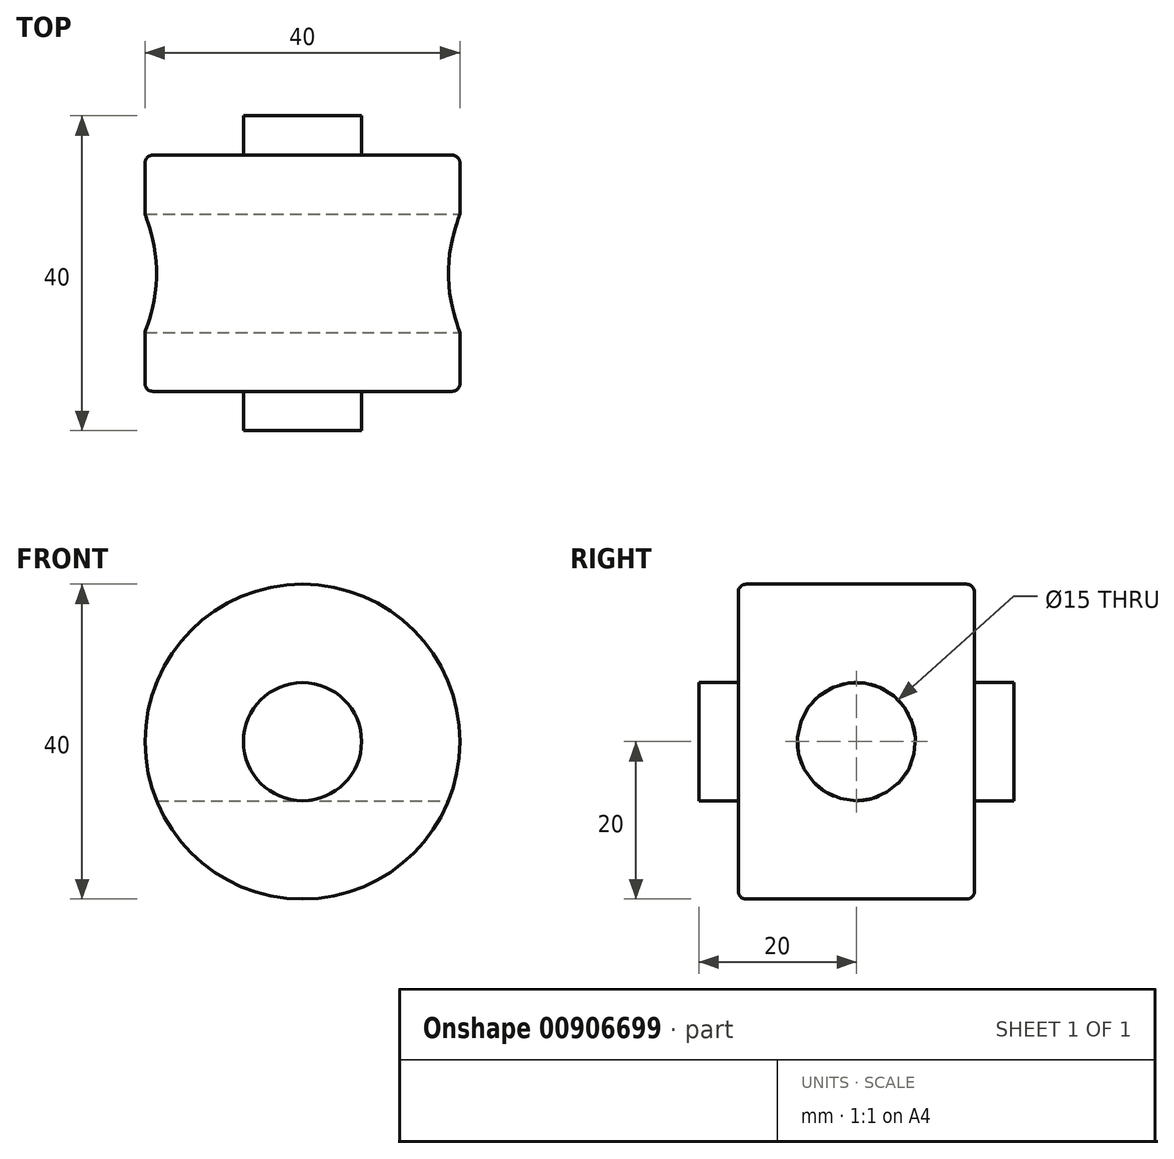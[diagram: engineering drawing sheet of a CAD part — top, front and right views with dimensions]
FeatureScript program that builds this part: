
annotation { "Feature Type Name" : "Feature", "Feature Type Description" : "" }
export const myFeature = defineFeature(function(context is Context, id is Id, definition is map)
    precondition{}
    {
        {
            var Q0;
            Q0=qCreatedBy(makeId("Front.planeOp"),FACE);
            var sketch = newSketch(context, id + "F0", { "sketchPlane" : qUnion([Q0])});
            skCircle(sketch, "E0", {"center": v(0, 0) * mm, "radius": 20 * mm});
            skCircle(sketch, "E1", {"center": v(0, 0) * mm, "radius": 7.5 * mm});
            skSolve(sketch);
        }
        {
            var Q0;
            Q0=makeQuery(id+"F0.imprint","IMPRINT",FACE,{"disambiguationData":[TD([[makeQuery(id+"F0.imprint","IMPRINT",EDGE,{"derivedFrom":sQuery(id+"F0.wireOp",EDGE,"E0")}),1.0]])]});
            extrude(context, id + "F1", {"entities" : qUnion([Q0]), "depth" : 30 * mm, "offsetDistance" : 25 * mm});
        }
        {
            var Q0;
            Q0=makeQuery(id+"F0.imprint","IMPRINT",FACE,{"disambiguationData":[TD([[makeQuery(id+"F0.imprint","IMPRINT",EDGE,{"derivedFrom":sQuery(id+"F0.wireOp",EDGE,"E1")}),1.0]])]});
            extrude(context, id + "F2", {"entities" : qUnion([Q0]), "operationType" : NewBodyOperationType.ADD, "depth" : 35 * mm, "offsetDistance" : 25 * mm, "hasSecondDirection" : true, "secondDirectionOppositeDirection" : true, "secondDirectionDepth" : 5 * mm});
        }
        {
            var Q0;
            Q0=qCreatedBy(makeId("Right.planeOp"),FACE);
            cPlane(context, id + "F3", {"entities" : qUnion([Q0]), "cplaneType" : CPlaneType.OFFSET, "offset" : 20 * mm, "width" : 150 * mm, "height" : 150 * mm});
        }
        {
            var Q0;
            Q0=qCreatedBy(id+"F3.planeOp",FACE);
            var sketch = newSketch(context, id + "F4", { "sketchPlane" : qUnion([Q0])});
            skCircle(sketch, "E2", {"center": v(-15, 0) * mm, "radius": 7.5 * mm});
            skSolve(sketch);
        }
        {
            var Q0;
            Q0=makeQuery(id+"F4.imprint","IMPRINT",FACE,{"disambiguationData":[TD([[makeQuery(id+"F4.imprint","IMPRINT",EDGE,{"derivedFrom":sQuery(id+"F4.wireOp",EDGE,"E2")}),1.0]])]});
            extrude(context, id + "F5", {"entities" : qUnion([Q0]), "operationType" : NewBodyOperationType.REMOVE, "endBound" : BoundingType.THROUGH_ALL, "oppositeDirection" : true, "depth" : 25 * mm, "offsetDistance" : 25 * mm});
        }
        {
            var Q0;
            Q0=makeQuery(id+"F1.opExtrude","CAP_EDGE",EDGE,{"disambiguationData":[OSD([sQuery(id+"F0.wireOp",EDGE,"E0")])],"isStart":false});
            var Q1;
            Q1=makeQuery(id+"F1.opExtrude","CAP_EDGE",EDGE,{"disambiguationData":[OSD([sQuery(id+"F0.wireOp",EDGE,"E0")])],"isStart":true});
            fillet(context, id + "F6", {"entities" : qUnion([Q0, Q1]), "radius" : 1 * mm, "tangentPropagation" : true, "allowEdgeOverflow" : false});
        }
    });
